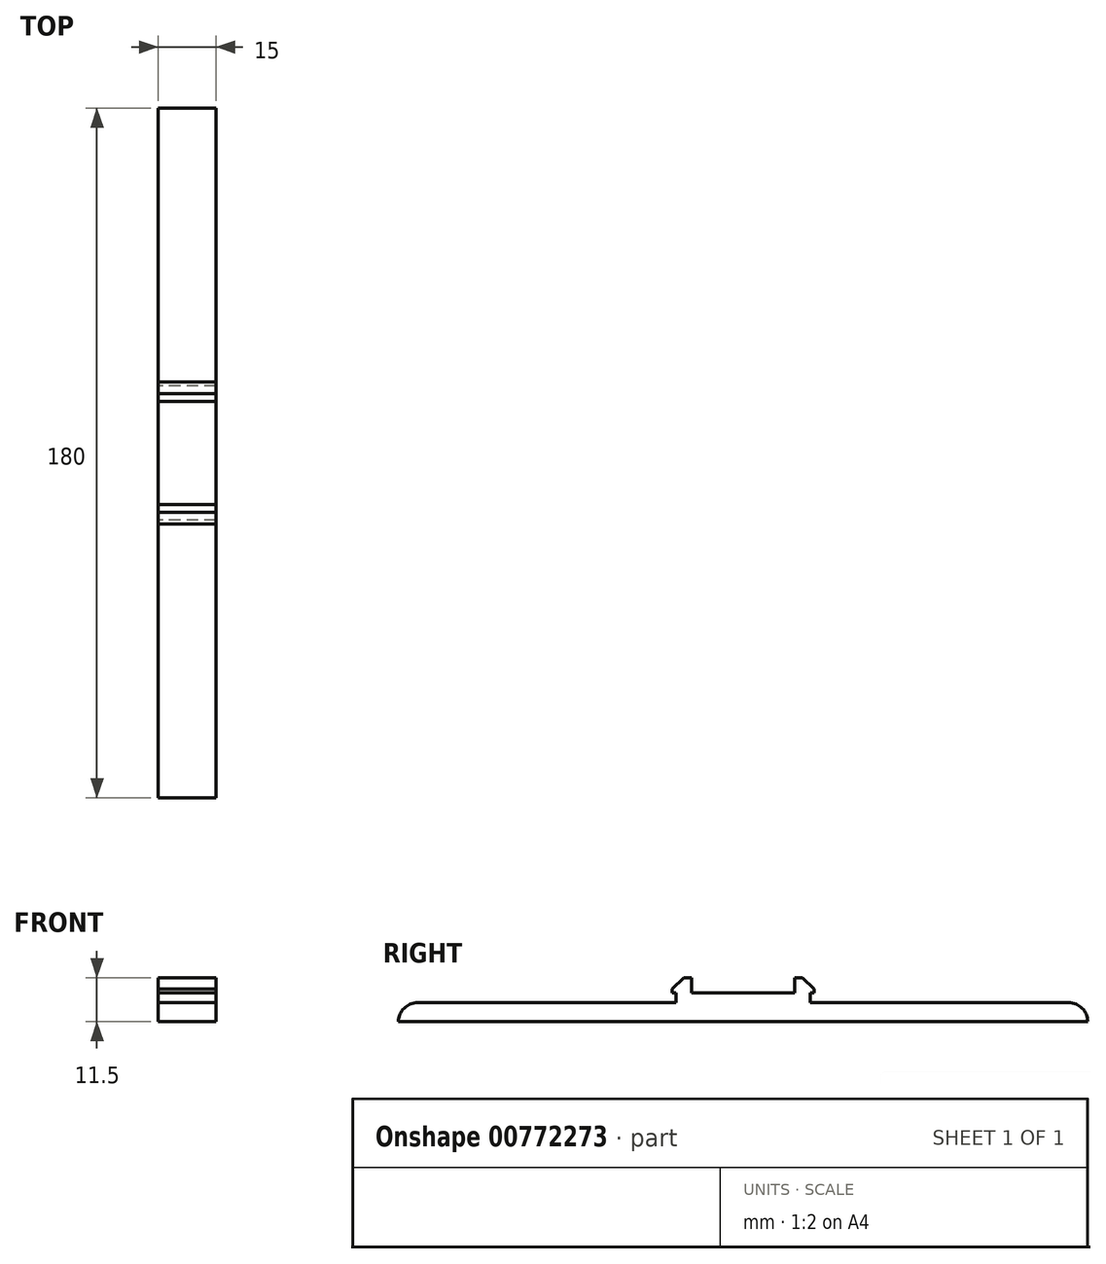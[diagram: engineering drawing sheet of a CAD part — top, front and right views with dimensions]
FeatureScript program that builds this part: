
annotation { "Feature Type Name" : "Feature", "Feature Type Description" : "" }
export const myFeature = defineFeature(function(context is Context, id is Id, definition is map)
    precondition{}
    {
        {
            var Q0;
            Q0=qCreatedBy(makeId("Right.planeOp"),FACE);
            var sketch = newSketch(context, id + "F0", { "sketchPlane" : qUnion([Q0])});
            skLineSegment(sketch, "E0.bottom", {"start": v(90, 5) * mm, "end": v(-90, 5) * mm});
            skLineSegment(sketch, "E0.top", {"start": v(90, 0) * mm, "end": v(-90, 0) * mm});
            skLineSegment(sketch, "E0.left", {"start": v(90, 5) * mm, "end": v(90, 0) * mm});
            skLineSegment(sketch, "E0.right", {"start": v(-90, 5) * mm, "end": v(-90, 0) * mm});
            skLineSegment(sketch, "E1.bottom", {"start": v(17.5, 5) * mm, "end": v(-17.5, 5) * mm});
            skLineSegment(sketch, "E1.top", {"start": v(17.5, 7.5) * mm, "end": v(-17.5, 7.5) * mm});
            skLineSegment(sketch, "E1.left", {"start": v(17.5, 5) * mm, "end": v(17.5, 7.5) * mm});
            skLineSegment(sketch, "E1.right", {"start": v(-17.5, 5) * mm, "end": v(-17.5, 7.5) * mm});
            skLineSegment(sketch, "E2.bottom", {"start": v(13.5, 7.5) * mm, "end": v(18.5, 7.5) * mm});
            skLineSegment(sketch, "E2.top", {"start": v(13.5, 11.5) * mm, "end": v(18.5, 11.5) * mm});
            skLineSegment(sketch, "E2.left", {"start": v(13.5, 7.5) * mm, "end": v(13.5, 11.5) * mm});
            skLineSegment(sketch, "E2.right", {"start": v(18.5, 7.5) * mm, "end": v(18.5, 11.5) * mm});
            skLineSegment(sketch, "E3.bottom", {"start": v(-13.5, 7.5) * mm, "end": v(-18.5, 7.5) * mm});
            skLineSegment(sketch, "E3.top", {"start": v(-13.5, 11.5) * mm, "end": v(-18.5, 11.5) * mm});
            skLineSegment(sketch, "E3.left", {"start": v(-13.5, 7.5) * mm, "end": v(-13.5, 11.5) * mm});
            skLineSegment(sketch, "E3.right", {"start": v(-18.5, 7.5) * mm, "end": v(-18.5, 11.5) * mm});
            skSolve(sketch);
        }
        {
            var Q0;
            {var subQ0=sQuery(id+"F0.wireOp",EDGE,"E2.bottom");Q0=makeQuery(id+"F0.imprint","IMPRINT",FACE,{"disambiguationData":[TD([[makeQuery(id+"F0.imprint","IMPRINT",EDGE,{"derivedFrom":subQ0}),1.0]])]});}
            var Q1;
            {var subQ2=sQuery(id+"F0.wireOp",EDGE,"E1.left");Q1=makeQuery(id+"F0.imprint","IMPRINT",FACE,{"disambiguationData":[TD([[makeQuery(id+"F0.imprint","IMPRINT",EDGE,{"derivedFrom":subQ2}),1.0]])]});}
            var Q2;
            Q2=makeQuery(id+"F0.imprint","IMPRINT",FACE,{"disambiguationData":[TD([[makeQuery(id+"F0.imprint","IMPRINT",EDGE,{"derivedFrom":sQuery(id+"F0.wireOp",EDGE,"E0.top")}),-1.0]])]});
            var Q3;
            {var subQ0=sQuery(id+"F0.wireOp",EDGE,"E3.bottom");Q3=makeQuery(id+"F0.imprint","IMPRINT",FACE,{"disambiguationData":[TD([[makeQuery(id+"F0.imprint","IMPRINT",EDGE,{"derivedFrom":subQ0}),-1.0]])]});}
            extrude(context, id + "F1", {"entities" : qUnion([Q0, Q1, Q2, Q3]), "depth" : 15 * mm, "offsetDistance" : 25 * mm});
        }
        {
            var Q0;
            Q0=makeQuery(id+"F1.opExtrude","SWEPT_EDGE",EDGE,{"disambiguationData":[OSD([sQuery(id+"F0.wireOp",EDGE,"E3.top"),sQuery(id+"F0.wireOp",EDGE,"E3.right")])]});
            var Q1;
            Q1=makeQuery(id+"F1.opExtrude","SWEPT_EDGE",EDGE,{"disambiguationData":[OSD([sQuery(id+"F0.wireOp",EDGE,"E2.top"),sQuery(id+"F0.wireOp",EDGE,"E2.right")])]});
            chamfer(context, id + "F2", {"entities" : qUnion([Q0, Q1]), "width" : 3 * mm, "tangentPropagation" : true});
        }
        {
            var Q0;
            Q0=makeQuery(id+"F1.opExtrude","SWEPT_EDGE",EDGE,{"disambiguationData":[OSD([sQuery(id+"F0.wireOp",EDGE,"E0.bottom"),sQuery(id+"F0.wireOp",EDGE,"E0.left")])]});
            var Q1;
            Q1=makeQuery(id+"F1.opExtrude","SWEPT_EDGE",EDGE,{"disambiguationData":[OSD([sQuery(id+"F0.wireOp",EDGE,"E0.bottom"),sQuery(id+"F0.wireOp",EDGE,"E0.right")])]});
            fillet(context, id + "F3", {"entities" : qUnion([Q0, Q1]), "radius" : 5 * mm, "tangentPropagation" : true, "allowEdgeOverflow" : false});
        }
    });
